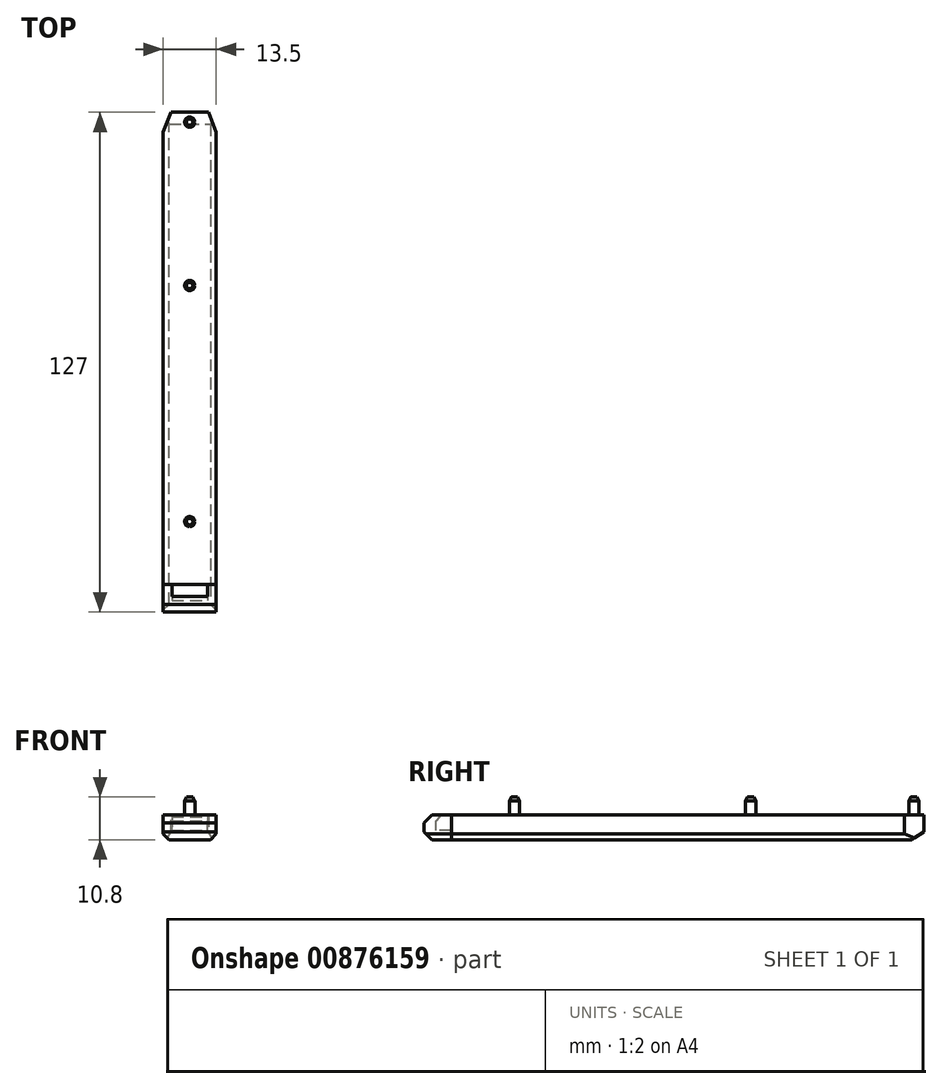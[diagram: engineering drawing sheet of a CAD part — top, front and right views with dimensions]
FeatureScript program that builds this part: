
annotation { "Feature Type Name" : "Feature", "Feature Type Description" : "" }
export const myFeature = defineFeature(function(context is Context, id is Id, definition is map)
    precondition{}
    {
        {
            var Q0;
            Q0=qCreatedBy(makeId("Top.planeOp"),FACE);
            var sketch = newSketch(context, id + "F0", { "sketchPlane" : qUnion([Q0])});
            skLineSegment(sketch, "E0.bottom", {"start": v(6.75, -60) * mm, "end": v(-6.75, -60) * mm});
            skLineSegment(sketch, "E0.top", {"start": v(6.75, 60) * mm, "end": v(-6.75, 60) * mm});
            skLineSegment(sketch, "E0.left", {"start": v(6.75, -60) * mm, "end": v(6.75, 60) * mm});
            skLineSegment(sketch, "E0.right", {"start": v(-6.75, -60) * mm, "end": v(-6.75, 60) * mm});
            skPoint(sketch, "E0.middle", {"position": v(0, 0) * mm});
            skSolve(sketch);
        }
        {
            var Q0;
            Q0=makeQuery(id+"F0.imprint","IMPRINT",FACE,{"disambiguationData":[TD([[makeQuery(id+"F0.imprint","IMPRINT",EDGE,{"derivedFrom":sQuery(id+"F0.wireOp",EDGE,"E0.bottom")}),-1.0]])]});
            extrude(context, id + "F1", {"entities" : qUnion([Q0]), "depth" : 6.3 * mm});
        }
        {
            var Q0;
            Q0=makeQuery(id+"F1.opExtrude","CAP_FACE",FACE,{"disambiguationData":[OSD([sQuery(id+"F0.wireOp",EDGE,"E0.bottom"),sQuery(id+"F0.wireOp",EDGE,"E0.top"),sQuery(id+"F0.wireOp",EDGE,"E0.left"),sQuery(id+"F0.wireOp",EDGE,"E0.right")])],"isStart":false});
            var sketch = newSketch(context, id + "F2", { "sketchPlane" : qUnion([Q0])});
            skLineSegment(sketch, "E1", {"start": v(0, -60) * mm, "end": v(0, 60) * mm, "construction": true});
            skCircle(sketch, "E2", {"center": v(0, 16) * mm, "radius": 1.3 * mm});
            skCircle(sketch, "E3", {"center": v(0, -44) * mm, "radius": 1.3 * mm});
            skCircle(sketch, "E4", {"center": v(0, 57.5) * mm, "radius": 1.3 * mm});
            skSolve(sketch);
        }
        {
            var Q0;
            Q0=makeQuery(id+"F2.imprint","IMPRINT",FACE,{"disambiguationData":[TD([[makeQuery(id+"F2.imprint","IMPRINT",EDGE,{"derivedFrom":sQuery(id+"F2.wireOp",EDGE,"E4")}),1.0]])]});
            var Q1;
            Q1=makeQuery(id+"F2.imprint","IMPRINT",FACE,{"disambiguationData":[TD([[makeQuery(id+"F2.imprint","IMPRINT",EDGE,{"derivedFrom":sQuery(id+"F2.wireOp",EDGE,"E2")}),1.0]])]});
            var Q2;
            Q2=makeQuery(id+"F2.imprint","IMPRINT",FACE,{"disambiguationData":[TD([[makeQuery(id+"F2.imprint","IMPRINT",EDGE,{"derivedFrom":sQuery(id+"F2.wireOp",EDGE,"E3")}),1.0]])]});
            extrude(context, id + "F3", {"entities" : qUnion([Q0, Q1, Q2]), "operationType" : NewBodyOperationType.ADD, "depth" : 4.5 * mm});
        }
        {
            var Q0;
            Q0=makeQuery(id+"F1.opExtrude","SWEPT_EDGE",EDGE,{"disambiguationData":[OSD([sQuery(id+"F0.wireOp",EDGE,"E0.top"),sQuery(id+"F0.wireOp",EDGE,"E0.left")])]});
            var Q1;
            Q1=makeQuery(id+"F1.opExtrude","SWEPT_EDGE",EDGE,{"disambiguationData":[OSD([sQuery(id+"F0.wireOp",EDGE,"E0.top"),sQuery(id+"F0.wireOp",EDGE,"E0.right")])]});
            chamfer(context, id + "F4", {"entities" : qUnion([Q0, Q1]), "chamferType" : ChamferType.TWO_OFFSETS, "width1" : 2 * mm, "oppositeDirection" : false, "width2" : 5 * mm, "tangentPropagation" : true});
        }
        {
            var Q0;
            Q0=makeQuery(id+"F3.opExtrude","CAP_EDGE",EDGE,{"disambiguationData":[OSD([sQuery(id+"F2.wireOp",EDGE,"E3")])],"isStart":false});
            var Q1;
            Q1=makeQuery(id+"F3.opExtrude","CAP_EDGE",EDGE,{"disambiguationData":[OSD([sQuery(id+"F2.wireOp",EDGE,"E2")])],"isStart":false});
            var Q2;
            Q2=makeQuery(id+"F3.opExtrude","CAP_EDGE",EDGE,{"disambiguationData":[OSD([sQuery(id+"F2.wireOp",EDGE,"E4")])],"isStart":false});
            chamfer(context, id + "F5", {"entities" : qUnion([Q0, Q1, Q2]), "chamferType" : ChamferType.TWO_OFFSETS, "width1" : 0.5 * mm, "oppositeDirection" : false, "width2" : 1 * mm, "tangentPropagation" : true});
        }
        {
            var Q0;
            Q0=makeQuery(id+"F1.opExtrude","SWEPT_FACE",FACE,{"disambiguationData":[OSD([sQuery(id+"F0.wireOp",EDGE,"E0.bottom")])]});
            var sketch = newSketch(context, id + "F6", { "sketchPlane" : qUnion([Q0])});
            skLineSegment(sketch, "E5.0.0", {"start": v(-6.75, 0) * mm, "end": v(6.75, 0) * mm});
            skLineSegment(sketch, "E5.0.1", {"start": v(6.75, 0) * mm, "end": v(6.75, 6.3) * mm});
            skLineSegment(sketch, "E5.0.2", {"start": v(6.75, 6.3) * mm, "end": v(-6.75, 6.3) * mm});
            skLineSegment(sketch, "E5.0.3", {"start": v(-6.75, 6.3) * mm, "end": v(-6.75, 0) * mm});
            skSolve(sketch);
        }
        {
            var Q0;
            Q0=makeQuery(id+"F6.imprint","IMPRINT",FACE,{"disambiguationData":[TD([[makeQuery(id+"F6.imprint","IMPRINT",EDGE,{"derivedFrom":sQuery(id+"F6.wireOp",EDGE,"E5.0.0")}),-1.0]])]});
            extrude(context, id + "F7", {"entities" : qUnion([Q0]), "depth" : 7 * mm});
        }
        {
            var Q0;
            Q0=qCreatedBy(makeId("Right.planeOp"),FACE);
            var sketch = newSketch(context, id + "F8", { "sketchPlane" : qUnion([Q0])});
            skLineSegment(sketch, "E6.0", {"start": v(-63, 6.3) * mm, "end": v(-60, 6.3) * mm});
            skLineSegment(sketch, "E7", {"start": v(-60, 6.3) * mm, "end": v(-60, 2.3) * mm});
            skLineSegment(sketch, "E8", {"start": v(-60, 2.3) * mm, "end": v(-64, 2.3) * mm});
            skLineSegment(sketch, "E9", {"start": v(-64, 2.3) * mm, "end": v(-64, 4.8) * mm});
            skPoint(sketch, "E10.orphan", {"position": v(-67, 6.3) * mm});
            skLineSegment(sketch, "E11", {"start": v(-63, 6.3) * mm, "end": v(-63, 5.8) * mm});
            skLineSegment(sketch, "E12", {"start": v(-63, 5.8) * mm, "end": v(-64, 4.8) * mm});
            skSolve(sketch);
        }
        {
            var Q0;
            Q0=qSketchRegion(id+"F8",true);
            extrude(context, id + "F9", {"entities" : qUnion([Q0]), "operationType" : NewBodyOperationType.REMOVE, "endBound" : BoundingType.SYMMETRIC, "oppositeDirection" : true, "depth" : (13 - 4) * mm});
        }
        {
            var Q0;
            Q0=makeQuery(id+"F7.opExtrude","CAP_EDGE",EDGE,{"disambiguationData":[OSD([sQuery(id+"F6.wireOp",EDGE,"E5.0.2")])],"isStart":false});
            var Q1;
            Q1=makeQuery(id+"F7.opExtrude","CAP_EDGE",EDGE,{"disambiguationData":[OSD([sQuery(id+"F6.wireOp",EDGE,"E5.0.0")])],"isStart":false});
            chamfer(context, id + "F10", {"entities" : qUnion([Q0, Q1]), "width" : 2 * mm, "tangentPropagation" : true});
        }
        {
            var Q0;
            Q0=makeQuery(id+"F1.opExtrude","CAP_EDGE",EDGE,{"disambiguationData":[OSD([sQuery(id+"F0.wireOp",EDGE,"E0.top")])],"isStart":true});
            chamfer(context, id + "F11", {"entities" : qUnion([Q0]), "chamferType" : ChamferType.TWO_OFFSETS, "width1" : 2 * mm, "oppositeDirection" : false, "width2" : 3 * mm, "tangentPropagation" : true});
        }
        {
            var Q0;
            Q0=makeQuery(id+"F1.opExtrude","CAP_EDGE",EDGE,{"disambiguationData":[OSD([sQuery(id+"F0.wireOp",EDGE,"E0.left")])],"isStart":true});
            var Q1;
            Q1=makeQuery(id+"F7.opExtrude","SWEPT_EDGE",EDGE,{"disambiguationData":[OSD([sQuery(id+"F6.wireOp",EDGE,"E5.0.0"),sQuery(id+"F6.wireOp",EDGE,"E5.0.1")])]});
            var Q2;
            Q2=makeQuery(id+"F7.opExtrude","SWEPT_EDGE",EDGE,{"disambiguationData":[OSD([sQuery(id+"F6.wireOp",EDGE,"E5.0.0"),sQuery(id+"F6.wireOp",EDGE,"E5.0.3")])]});
            var Q3;
            Q3=makeQuery(id+"F1.opExtrude","CAP_EDGE",EDGE,{"disambiguationData":[OSD([sQuery(id+"F0.wireOp",EDGE,"E0.right")])],"isStart":true});
            chamfer(context, id + "F12", {"entities" : qUnion([Q0, Q1, Q2, Q3]), "width" : 1.5 * mm, "tangentPropagation" : true});
        }
    });
